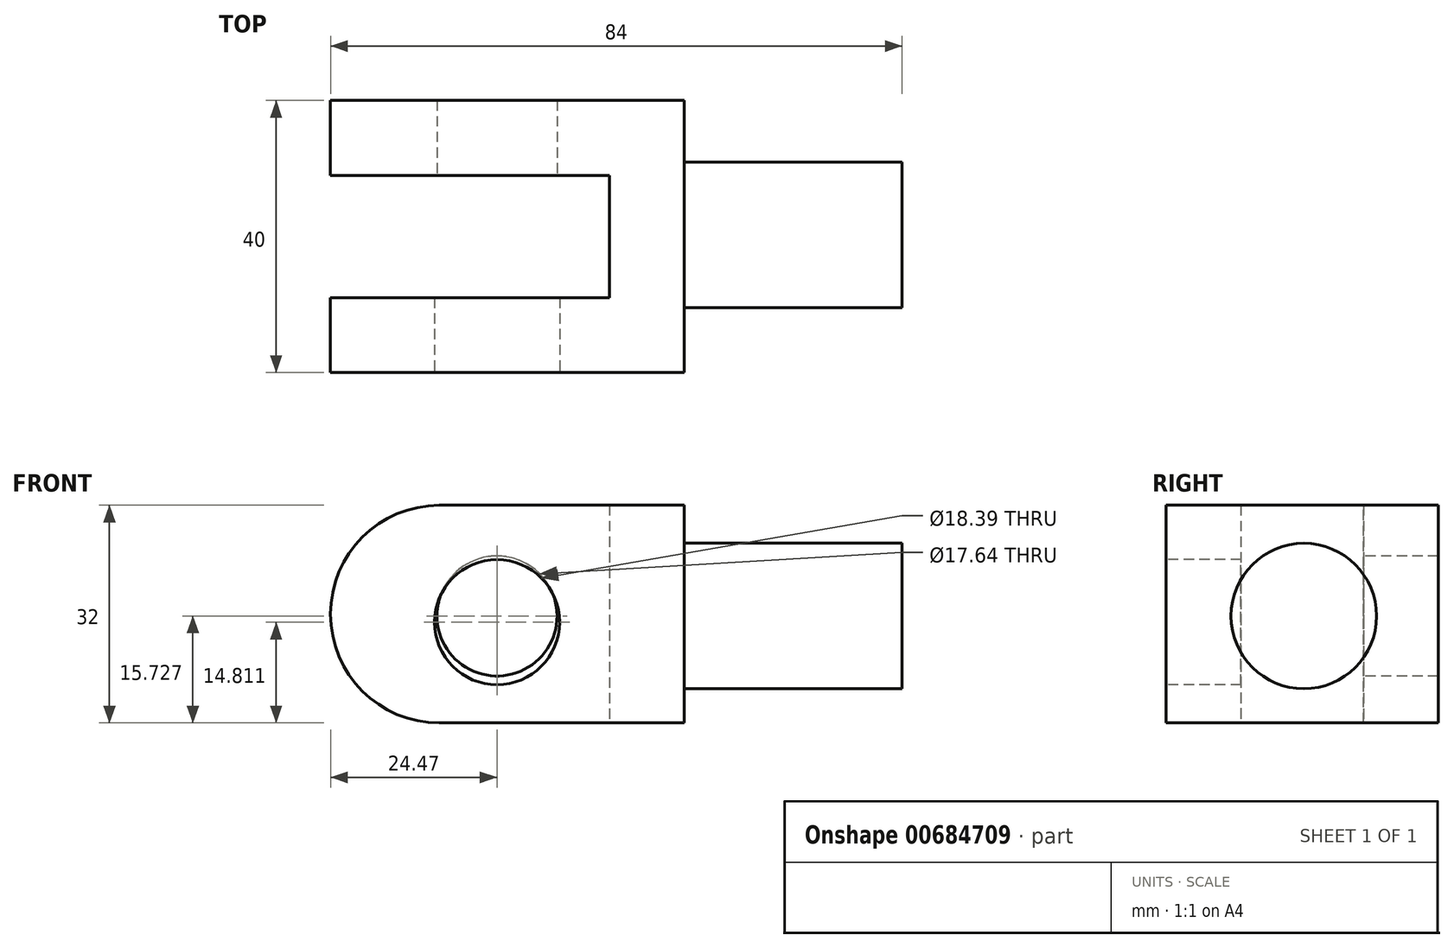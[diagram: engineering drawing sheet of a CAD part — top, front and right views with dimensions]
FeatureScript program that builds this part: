
annotation { "Feature Type Name" : "Feature", "Feature Type Description" : "" }
export const myFeature = defineFeature(function(context is Context, id is Id, definition is map)
    precondition{}
    {
        {
            var Q0;
            Q0=qCreatedBy(makeId("Top.planeOp"),FACE);
            var sketch = newSketch(context, id + "F0", { "sketchPlane" : qUnion([Q0])});
            skLineSegment(sketch, "E0", {"start": v(-24.47, 19.76) * mm, "end": v(16.53, 19.76) * mm});
            skLineSegment(sketch, "E1", {"start": v(-24.47, 19.76) * mm, "end": v(-24.47, 8.76) * mm});
            skLineSegment(sketch, "E2", {"start": v(-24.47, 8.76) * mm, "end": v(16.53, 8.76) * mm});
            skLineSegment(sketch, "E3", {"start": v(16.53, 8.76) * mm, "end": v(16.53, -9.24) * mm});
            skLineSegment(sketch, "E4", {"start": v(16.53, -9.24) * mm, "end": v(-24.47, -9.24) * mm});
            skLineSegment(sketch, "E5", {"start": v(-24.47, -9.24) * mm, "end": v(-24.47, -20.24) * mm});
            skLineSegment(sketch, "E6", {"start": v(-24.47, -20.24) * mm, "end": v(27.53, -20.24) * mm});
            skLineSegment(sketch, "E7", {"start": v(27.53, -20.24) * mm, "end": v(27.53, 19.76) * mm});
            skLineSegment(sketch, "E8", {"start": v(27.53, 19.76) * mm, "end": v(16.53, 19.76) * mm});
            skSolve(sketch);
        }
        {
            var Q0;
            Q0 = qSketchRegion(id + "F0", true);
            extrude(context, id + "F1", {"entities" : qUnion([Q0]), "depth" : 32 * mm, "offsetDistance" : 25.4 * mm});
        }
        {
            var Q0;
            Q0=makeQuery(id+"F1.opExtrude","SWEPT_FACE",FACE,{"disambiguationData":[OSD([sQuery(id+"F0.wireOp",EDGE,"E6")])]});
            var sketch = newSketch(context, id + "F2", { "sketchPlane" : qUnion([Q0])});
            skCircle(sketch, "E9", {"center": v(0, 14.81) * mm, "radius": 9.2 * mm});
            skSolve(sketch);
        }
        {
            var Q0;
            Q0=qCreatedBy(makeId("Front.planeOp"),FACE);
            var sketch = newSketch(context, id + "F3", { "sketchPlane" : qUnion([Q0])});
            skCircle(sketch, "E10", {"center": v(0, 15.73) * mm, "radius": 8.82 * mm});
            skSolve(sketch);
        }
        {
            var Q0;
            Q0 = qSketchRegion(id + "F2", true);
            extrude(context, id + "F4", {"entities" : qUnion([Q0]), "operationType" : NewBodyOperationType.REMOVE, "oppositeDirection" : true, "depth" : 11 * mm, "offsetDistance" : 25.4 * mm});
        }
        {
            var Q0;
            Q0 = qSketchRegion(id + "F3", true);
            extrude(context, id + "F5", {"entities" : qUnion([Q0]), "operationType" : NewBodyOperationType.REMOVE, "oppositeDirection" : true, "depth" : 50.8 * mm, "offsetDistance" : 25.4 * mm});
        }
        {
            var Q0;
            Q0=makeQuery(id+"F1.opExtrude","CAP_EDGE",EDGE,{"disambiguationData":[OSD([sQuery(id+"F0.wireOp",EDGE,"E5")])],"isStart":false});
            fillet(context, id + "F6", {"entities" : qUnion([Q0]), "radius" : 16 * mm, "tangentPropagation" : true, "allowEdgeOverflow" : false});
        }
        {
            var Q0;
            Q0=makeQuery(id+"F1.opExtrude","CAP_EDGE",EDGE,{"disambiguationData":[OSD([sQuery(id+"F0.wireOp",EDGE,"E5")])],"isStart":true});
            fillet(context, id + "F7", {"entities" : qUnion([Q0]), "radius" : 16 * mm, "tangentPropagation" : true, "allowEdgeOverflow" : false});
        }
        {
            var Q0;
            Q0=makeQuery(id+"F1.opExtrude","CAP_EDGE",EDGE,{"disambiguationData":[OSD([sQuery(id+"F0.wireOp",EDGE,"E1")])],"isStart":false});
            fillet(context, id + "F8", {"entities" : qUnion([Q0]), "radius" : 16 * mm, "tangentPropagation" : true, "allowEdgeOverflow" : false});
        }
        {
            var Q0;
            Q0=makeQuery(id+"F1.opExtrude","CAP_EDGE",EDGE,{"disambiguationData":[OSD([sQuery(id+"F0.wireOp",EDGE,"E1")])],"isStart":true});
            fillet(context, id + "F9", {"entities" : qUnion([Q0]), "radius" : 16 * mm, "tangentPropagation" : true, "allowEdgeOverflow" : false});
        }
        {
            var Q0;
            Q0=makeQuery(id+"F1.opExtrude","SWEPT_FACE",FACE,{"disambiguationData":[OSD([sQuery(id+"F0.wireOp",EDGE,"E7")])]});
            var sketch = newSketch(context, id + "F10", { "sketchPlane" : qUnion([Q0])});
            skCircle(sketch, "E11", {"center": v(0, 15.73) * mm, "radius": 10.7 * mm});
            skSolve(sketch);
        }
        {
            var Q0;
            Q0 = qSketchRegion(id + "F10", true);
            extrude(context, id + "F11", {"entities" : qUnion([Q0]), "operationType" : NewBodyOperationType.ADD, "depth" : 32 * mm, "offsetDistance" : 25.4 * mm});
        }
    });
